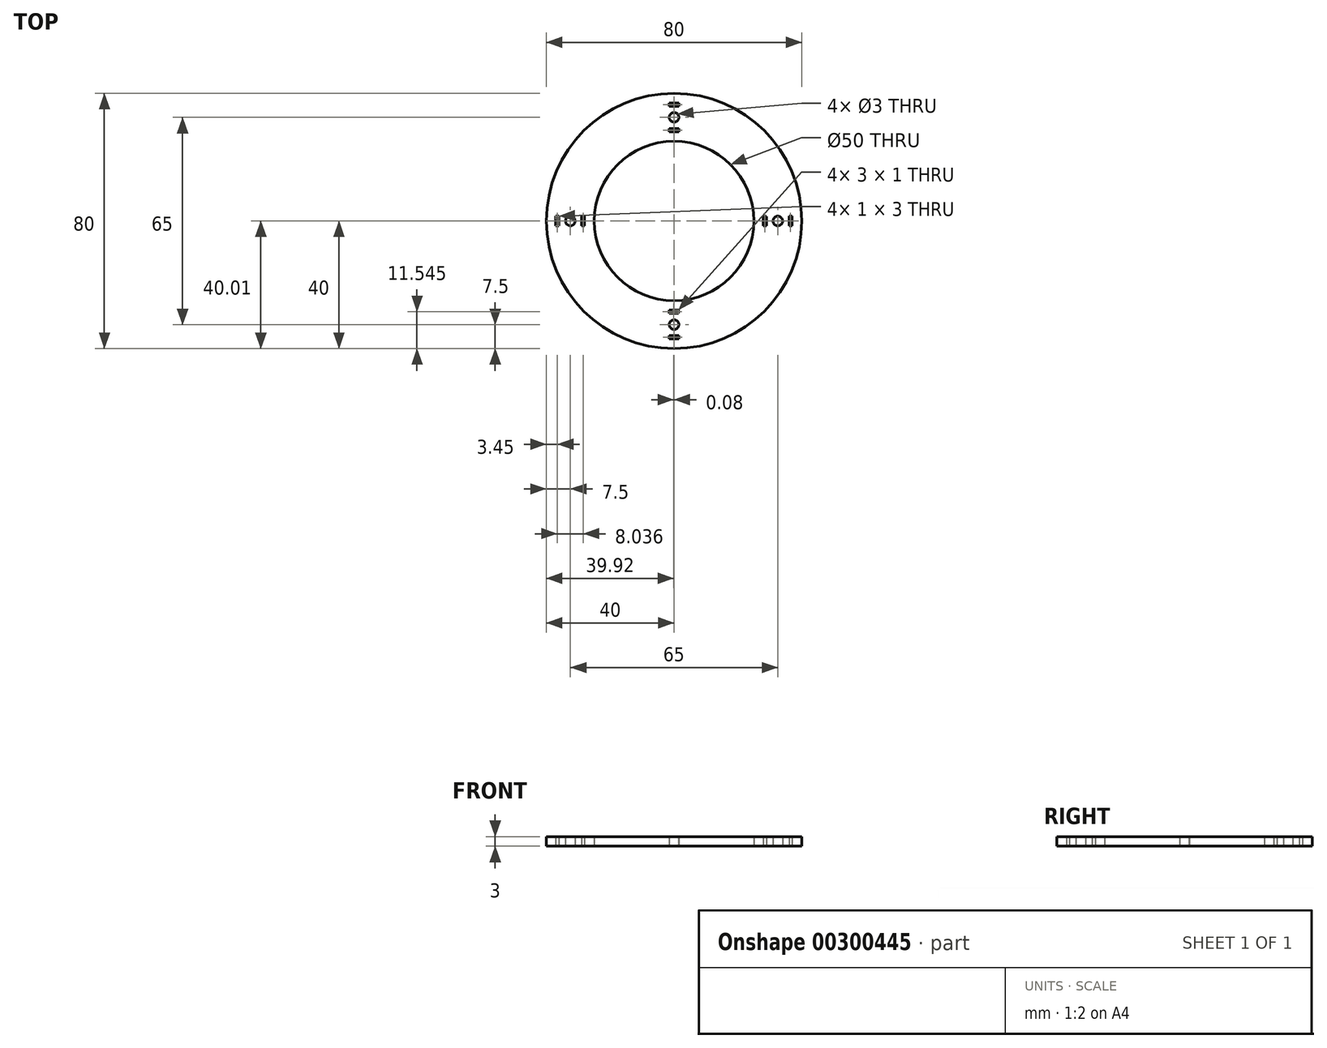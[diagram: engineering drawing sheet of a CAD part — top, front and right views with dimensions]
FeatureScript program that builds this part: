
annotation { "Feature Type Name" : "Feature", "Feature Type Description" : "" }
export const myFeature = defineFeature(function(context is Context, id is Id, definition is map)
    precondition{}
    {
        {
            var Q0;
            Q0=qCreatedBy(makeId("Top.planeOp"),FACE);
            var sketch = newSketch(context, id + "F0", { "sketchPlane" : qUnion([Q0])});
            skCircle(sketch, "E0", {"center": v(0, 0) * mm, "radius": 40 * mm});
            skCircle(sketch, "E1", {"center": v(0, 0) * mm, "radius": 25 * mm});
            skCircle(sketch, "E2", {"center": v(0, 32.5) * mm, "radius": 1.5 * mm});
            skCircle(sketch, "E3", {"center": v(-32.5, 0) * mm, "radius": 1.5 * mm});
            skCircle(sketch, "E4", {"center": v(0, -32.5) * mm, "radius": 1.5 * mm});
            skCircle(sketch, "E5", {"center": v(32.5, 0) * mm, "radius": 1.5 * mm});
            skLineSegment(sketch, "E6", {"start": v(0, 29) * mm, "end": v(-1.5, 29) * mm});
            skLineSegment(sketch, "E7", {"start": v(-1.5, 29) * mm, "end": v(-1.5, 28) * mm});
            skLineSegment(sketch, "E8", {"start": v(-1.5, 28) * mm, "end": v(1.5, 28) * mm});
            skLineSegment(sketch, "E9", {"start": v(1.5, 28) * mm, "end": v(1.5, 29) * mm});
            skLineSegment(sketch, "E10", {"start": v(1.5, 29) * mm, "end": v(0, 29) * mm});
            skLineSegment(sketch, "E11", {"start": v(0, 36) * mm, "end": v(1.5, 36) * mm});
            skLineSegment(sketch, "E12", {"start": v(1.5, 36) * mm, "end": v(1.5, 37) * mm});
            skLineSegment(sketch, "E13", {"start": v(1.5, 37) * mm, "end": v(-1.5, 37) * mm});
            skLineSegment(sketch, "E14", {"start": v(-1.5, 37) * mm, "end": v(-1.5, 36) * mm});
            skLineSegment(sketch, "E15", {"start": v(0, -35.97) * mm, "end": v(-1.5, -35.97) * mm});
            skLineSegment(sketch, "E16", {"start": v(-1.5, -35.97) * mm, "end": v(-1.5, -36.97) * mm});
            skLineSegment(sketch, "E17", {"start": v(-1.5, -36.97) * mm, "end": v(1.5, -36.97) * mm});
            skLineSegment(sketch, "E18", {"start": v(1.5, -36.97) * mm, "end": v(1.5, -35.97) * mm});
            skLineSegment(sketch, "E19", {"start": v(1.5, -35.97) * mm, "end": v(0, -35.97) * mm});
            skLineSegment(sketch, "E20", {"start": v(-0.08, -28.96) * mm, "end": v(1.42, -28.96) * mm});
            skLineSegment(sketch, "E21", {"start": v(1.42, -28.96) * mm, "end": v(1.42, -27.96) * mm});
            skLineSegment(sketch, "E22", {"start": v(1.42, -27.96) * mm, "end": v(-1.58, -27.96) * mm});
            skLineSegment(sketch, "E23", {"start": v(-1.58, -27.96) * mm, "end": v(-1.58, -28.96) * mm});
            skLineSegment(sketch, "E24", {"start": v(-1.58, -28.96) * mm, "end": v(-0.08, -28.96) * mm});
            skLineSegment(sketch, "E25", {"start": v(36, 0.02) * mm, "end": v(36, -1.48) * mm});
            skLineSegment(sketch, "E26", {"start": v(36, -1.48) * mm, "end": v(37, -1.48) * mm});
            skLineSegment(sketch, "E27", {"start": v(37, -1.48) * mm, "end": v(37, 1.52) * mm});
            skLineSegment(sketch, "E28", {"start": v(37, 1.52) * mm, "end": v(36, 1.52) * mm});
            skLineSegment(sketch, "E29", {"start": v(36, 1.52) * mm, "end": v(36, 0.02) * mm});
            skLineSegment(sketch, "E30", {"start": v(28.96, -0.04) * mm, "end": v(28.96, 1.46) * mm});
            skLineSegment(sketch, "E31", {"start": v(28.96, 1.46) * mm, "end": v(27.96, 1.46) * mm});
            skLineSegment(sketch, "E32", {"start": v(27.96, 1.46) * mm, "end": v(27.96, -1.54) * mm});
            skLineSegment(sketch, "E33", {"start": v(27.96, -1.54) * mm, "end": v(28.96, -1.54) * mm});
            skLineSegment(sketch, "E34", {"start": v(28.96, -1.54) * mm, "end": v(28.96, -0.04) * mm});
            skLineSegment(sketch, "E35", {"start": v(-29.01, -0.01) * mm, "end": v(-29.01, -1.51) * mm});
            skLineSegment(sketch, "E36", {"start": v(-29.01, -1.51) * mm, "end": v(-28.01, -1.51) * mm});
            skLineSegment(sketch, "E37", {"start": v(-28.01, -1.51) * mm, "end": v(-28.01, 1.49) * mm});
            skLineSegment(sketch, "E38", {"start": v(-28.01, 1.49) * mm, "end": v(-29.01, 1.49) * mm});
            skLineSegment(sketch, "E39", {"start": v(-29.01, 1.49) * mm, "end": v(-29.01, -0.01) * mm});
            skLineSegment(sketch, "E40", {"start": v(-36.05, 0.01) * mm, "end": v(-36.05, 1.51) * mm});
            skLineSegment(sketch, "E41", {"start": v(-36.05, 1.51) * mm, "end": v(-37.05, 1.51) * mm});
            skLineSegment(sketch, "E42", {"start": v(-37.05, 1.51) * mm, "end": v(-37.05, -1.49) * mm});
            skLineSegment(sketch, "E43", {"start": v(-37.05, -1.49) * mm, "end": v(-36.05, -1.49) * mm});
            skLineSegment(sketch, "E44", {"start": v(-36.05, -1.49) * mm, "end": v(-36.05, 0.01) * mm});
            skLineSegment(sketch, "E45", {"start": v(0, 36) * mm, "end": v(-1.5, 36) * mm});
            skSolve(sketch);
        }
        {
            var Q0;
            Q0 = qSketchRegion(id + "F0", true);
            extrude(context, id + "F1", {"entities" : qUnion([Q0]), "depth" : 3 * mm});
        }
    });
